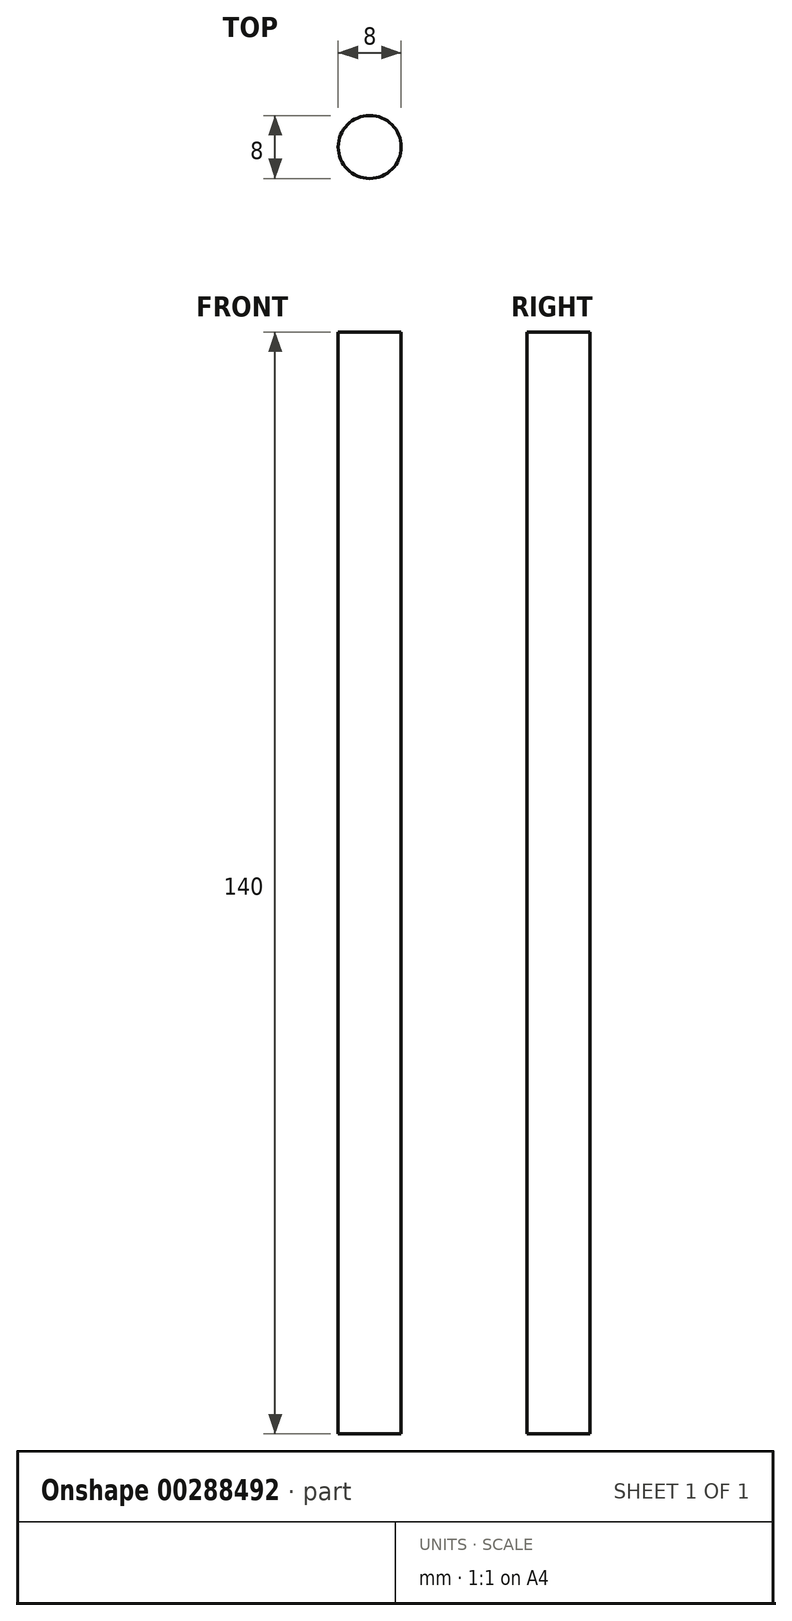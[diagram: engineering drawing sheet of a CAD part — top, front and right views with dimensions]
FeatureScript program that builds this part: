
annotation { "Feature Type Name" : "Feature", "Feature Type Description" : "" }
export const myFeature = defineFeature(function(context is Context, id is Id, definition is map)
    precondition{}
    {
        {
            var Q0;
            Q0=qCreatedBy(makeId("Front.planeOp"),FACE);
            var sketch = newSketch(context, id + "F0", { "sketchPlane" : qUnion([Q0])});
            skLineSegment(sketch, "E0.bottom", {"start": v(0, 110.92) * mm, "end": v(-4, 110.92) * mm});
            skLineSegment(sketch, "E0.top", {"start": v(0, -29.08) * mm, "end": v(-4, -29.08) * mm});
            skLineSegment(sketch, "E0.left", {"start": v(0, 110.92) * mm, "end": v(0, -29.08) * mm});
            skLineSegment(sketch, "E0.right", {"start": v(-4, 110.92) * mm, "end": v(-4, -29.08) * mm});
            skSolve(sketch);
        }
        {
            var Q0;
            Q0=makeQuery(id+"F0.imprint","IMPRINT",FACE,{"disambiguationData":[TD([[makeQuery(id+"F0.imprint","IMPRINT",EDGE,{"derivedFrom":sQuery(id+"F0.wireOp",EDGE,"E0.bottom")}),1.0]])]});
            var Q1;
            Q1=sQuery(id+"F0.wireOp",EDGE,"E0.left");
            revolve(context, id + "F1", {"entities" : qUnion([Q0]), "axis" : qUnion([Q1]), "revolveType" : RevolveType.FULL});
        }
    });
